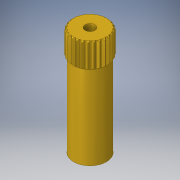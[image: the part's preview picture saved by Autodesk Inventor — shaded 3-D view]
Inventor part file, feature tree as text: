
AUTODESK INVENTOR PART (.ipt)
format: ipt  version: 2016 (Build 200138000, 138)  size: 364,032 bytes
history: native  units: mm
features: extrude x6, sketch x6, pattern_circular x2, plane x2, projected_geometry x2, other x1, mirror x1
ambient origin geometry x8: Origin, YZ Plane, XZ Plane, XY Plane, X Axis, Y Axis, Z Axis, Center Point
bodies: Body1 (feature_tree)
feature tree (20):
  other  "Sólido1"
  extrude  "Extrusión1"  Depth=13.5mm TaperAngle=0.0deg
  extrude  "Extrusión2"  Depth=4.0mm TaperAngle=0.0deg
  extrude  "Extrusión3"  Depth=4.0mm TaperAngle=360.0deg
  pattern_circular  "Patrón circular1"  Angle=45.0deg  [1 undecoded]
  plane  "Plano de trabajo1"
  extrude  "Extrusión4"  Depth=13.5mm
  pattern_circular  "Patrón circular2"  [2 undecoded]
  extrude  "Extrusión5"  Depth=13.5mm TaperAngle=360.0deg
  extrude  "Extrusión6"  Depth=13.5mm
  plane  "Plano de trabajo3"
  mirror  "Simetría2"
  sketch  "Boceto1"  dims[d0=5.8mm d1=13.5mm d2=0.0mm]
  sketch  "Boceto2"  dims[d3=0.3mm d4=4.0mm d5=0.0mm]
  projected_geometry  "Contorno proyectado1"
  sketch  "Boceto3"  dims[d9=4.0mm d10=0.0mm d11=260.0mm d12=360.0deg]
  projected_geometry  "Contorno proyectado2"
  sketch  "Boceto5"  dims[d21=0.3mm]
  sketch  "Boceto6"  dims[d22=13.962634mm]
  sketch  "Boceto7"  dims[d23=8.726646mm d25=45.0deg d26=0.25mm d27=0.7mm d28=0.0mm d29=260.0mm d30=360.0deg d32=1.6mm d33=4.0mm d34=0.0mm d36=13.5mm d37=0.0mm d38=5.3mm]
note: 3 required parameter values undecoded (feature->parameter linkage not recoverable at this tier; creation-order binding heuristic only, values carry confidence <= 0.55)
